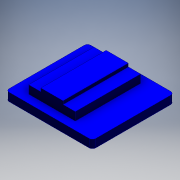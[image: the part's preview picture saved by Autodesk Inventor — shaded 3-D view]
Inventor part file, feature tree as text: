
AUTODESK INVENTOR PART (.ipt)
format: ipt  version: 2016 (Build 200138000, 138)  size: 166,912 bytes
history: native  units: mm
features: extrude x4, sketch x4
ambient origin geometry x8: Origin, YZ Plane, XZ Plane, XY Plane, X Axis, Y Axis, Z Axis, Center Point
bodies: Solid1 (feature_tree)
feature tree (8):
  extrude  "base"  Depth=53.0mm
  extrude  "magnetExt"  Depth=2.0mm
  extrude  "spacerOne"  Depth=50.0mm
  extrude  "sample"  Depth=2.0mm
  sketch  "Sketch1"  dims[d0=53.0mm d1=53.0mm]
  sketch  "Sketch3"  dims[d2=2.0mm d3=25.0mm]
  sketch  "Sketch7"  dims[d4=50.0mm d5=26.5mm]
  sketch  "Sketch8"  dims[d6=5.0mm d7=0.0mm d14=15.0mm d15=15.0mm d16=15.0mm d17=15.0mm d18=15.0mm d56=5.65mm d57=5.65mm d58=5.65mm d59=5.65mm d60=5.65mm d61=2.5mm d62=0.0mm d70=40.0mm d71=20.0mm d72=28.6mm d73=8.9mm d74=5.0mm d75=0.0mm d76=40.0mm d77=20.0mm d78=13.6mm d79=30.0mm d80=2.0mm d81=0.0mm]
